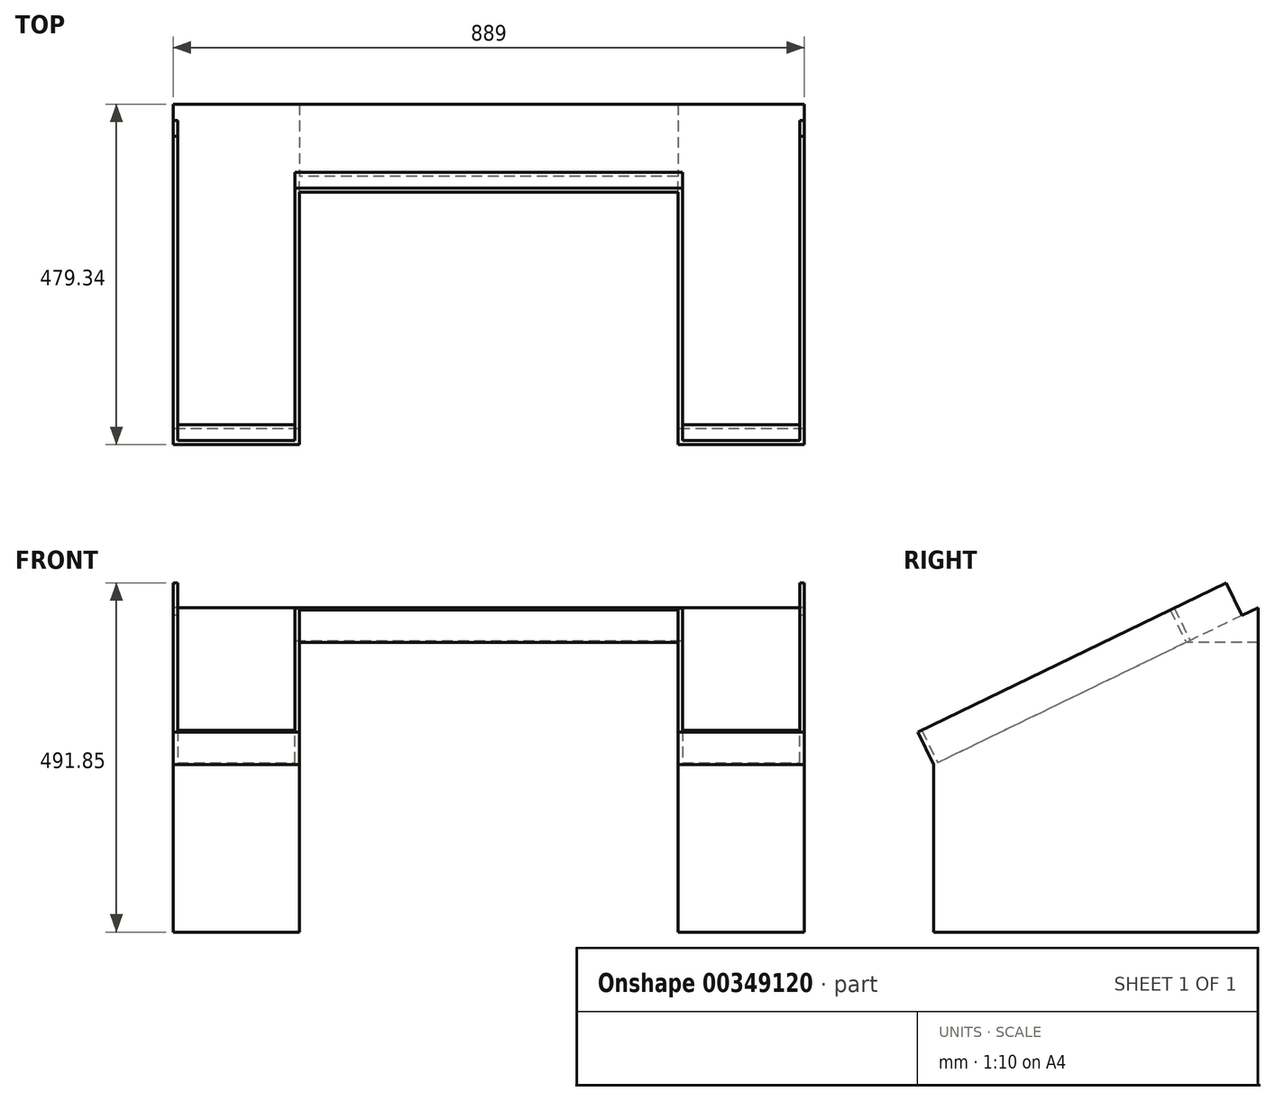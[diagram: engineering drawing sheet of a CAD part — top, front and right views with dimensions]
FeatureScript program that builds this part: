
annotation { "Feature Type Name" : "Feature", "Feature Type Description" : "" }
export const myFeature = defineFeature(function(context is Context, id is Id, definition is map)
    precondition{}
    {
        {
            var Q0;
            Q0=qCreatedBy(makeId("Right.planeOp"),FACE);
            var sketch = newSketch(context, id + "F0", { "sketchPlane" : qUnion([Q0])});
            skLineSegment(sketch, "E0.right", {"start": v(0, 221.43) * mm, "end": v(0, -235.77) * mm});
            skLineSegment(sketch, "E1", {"start": v(0, 221.43) * mm, "end": v(-457.2, 0) * mm});
            skLineSegment(sketch, "E2.right", {"start": v(-457.2, 43.63) * mm, "end": v(-457.2, -235.77) * mm});
            skLineSegment(sketch, "E3", {"start": v(0, -235.77) * mm, "end": v(-457.2, -235.77) * mm});
            skSolve(sketch);
        }
        {
            var Q0;
            Q0 = qSketchRegion(id + "F0", true);
            extrude(context, id + "F1", {"entities" : qUnion([Q0]), "depth" : 889 * mm});
        }
        {
            var Q0;
            Q0=makeQuery(id+"F1.opExtrude","SWEPT_FACE",FACE,{"disambiguationData":[OSD([sQuery(id+"F0.wireOp",EDGE,"E2.right")])]});
            var sketch = newSketch(context, id + "F2", { "sketchPlane" : qUnion([Q0])});
            skLineSegment(sketch, "E4.bottom", {"start": v(177.8, -235.77) * mm, "end": v(711.2, -235.77) * mm});
            skLineSegment(sketch, "E4.top", {"start": v(177.8, 224.7) * mm, "end": v(711.2, 224.7) * mm});
            skLineSegment(sketch, "E4.left", {"start": v(177.8, -235.77) * mm, "end": v(177.8, 224.7) * mm});
            skLineSegment(sketch, "E4.right", {"start": v(711.2, -235.77) * mm, "end": v(711.2, 224.7) * mm});
            skSolve(sketch);
        }
        {
            var Q0;
            {var subQ0=sQuery(id+"F2.wireOp",EDGE,"E4.bottom");Q0=makeQuery(id+"F2.imprint","IMPRINT",FACE,{"disambiguationData":[TD([[makeQuery(id+"F2.imprint","IMPRINT",EDGE,{"derivedFrom":subQ0}),-1.0]])]});}
            var Q1;
            {var subQ0=sQuery(id+"F2.wireOp",EDGE,"E4.top");Q1=makeQuery(id+"F2.imprint","IMPRINT",FACE,{"disambiguationData":[TD([[makeQuery(id+"F2.imprint","IMPRINT",EDGE,{"derivedFrom":subQ0}),-1.0]])]});}
            extrude(context, id + "F3", {"entities" : qUnion([Q0, Q1]), "operationType" : NewBodyOperationType.REMOVE, "oppositeDirection" : true, "depth" : 355.6 * mm});
        }
        {
            var Q0;
            Q0=makeQuery(id+"F1.opExtrude","SWEPT_FACE",FACE,{"disambiguationData":[OSD([sQuery(id+"F0.wireOp",EDGE,"E1")])]});
            var sketch = newSketch(context, id + "F4", { "sketchPlane" : qUnion([Q0])});
            skLineSegment(sketch, "E5", {"start": v(0, 96.52) * mm, "end": v(889, 96.52) * mm});
            skLineSegment(sketch, "E6", {"start": v(889, 96.52) * mm, "end": v(889, -411.48) * mm});
            skLineSegment(sketch, "E7", {"start": v(889, -411.48) * mm, "end": v(711.2, -411.48) * mm});
            skLineSegment(sketch, "E8", {"start": v(711.2, -411.48) * mm, "end": v(711.2, -16.37) * mm});
            skLineSegment(sketch, "E9", {"start": v(711.2, -16.37) * mm, "end": v(177.8, -16.37) * mm});
            skLineSegment(sketch, "E10", {"start": v(177.8, -16.37) * mm, "end": v(177.8, -411.48) * mm});
            skLineSegment(sketch, "E11", {"start": v(177.8, -411.48) * mm, "end": v(0, -411.48) * mm});
            skLineSegment(sketch, "E12", {"start": v(0, -411.48) * mm, "end": v(0, 96.52) * mm});
            skLineSegment(sketch, "E13", {"start": v(6.35, 90.17) * mm, "end": v(6.35, -405.13) * mm});
            skLineSegment(sketch, "E14", {"start": v(6.35, -405.13) * mm, "end": v(171.45, -405.13) * mm});
            skLineSegment(sketch, "E15", {"start": v(171.45, -405.13) * mm, "end": v(171.45, -10.02) * mm});
            skLineSegment(sketch, "E16", {"start": v(171.45, -10.02) * mm, "end": v(717.55, -10.02) * mm});
            skLineSegment(sketch, "E17", {"start": v(717.55, -10.02) * mm, "end": v(717.55, -405.13) * mm});
            skLineSegment(sketch, "E18", {"start": v(717.55, -405.13) * mm, "end": v(882.65, -405.13) * mm});
            skLineSegment(sketch, "E19", {"start": v(882.65, -405.13) * mm, "end": v(882.65, 90.17) * mm});
            skLineSegment(sketch, "E20", {"start": v(882.65, 90.17) * mm, "end": v(6.35, 90.17) * mm});
            skSolve(sketch);
        }
        {
            var Q0;
            Q0 = qSketchRegion(id + "F4", true);
            extrude(context, id + "F5", {"entities" : qUnion([Q0]), "operationType" : NewBodyOperationType.ADD, "depth" : 50.8 * mm});
        }
        {
            var Q0;
            Q0=makeQuery(id+"F5.opExtrude","SWEPT_FACE",FACE,{"disambiguationData":[OSD([sQuery(id+"F4.wireOp",EDGE,"E5")])]});
            extrude(context, id + "F6", {"entities" : qUnion([Q0]), "operationType" : NewBodyOperationType.REMOVE, "oppositeDirection" : true, "depth" : 25.4 * mm});
        }
        {
            var Q0;
            Q0=makeQuery(id+"F3.boolean.opBoolean","COPY",FACE,{"derivedFrom":makeQuery(id+"F3.opExtrude","CAP_FACE",FACE,{"disambiguationData":[OSD([sQuery(id+"F2.wireOp",EDGE,"E4.bottom"),sQuery(id+"F2.wireOp",EDGE,"E4.top"),sQuery(id+"F2.wireOp",EDGE,"E4.left"),sQuery(id+"F2.wireOp",EDGE,"E4.right")])],"isStart":false})});
            extrude(context, id + "F7", {"entities" : qUnion([Q0]), "operationType" : NewBodyOperationType.REMOVE, "endBound" : BoundingType.THROUGH_ALL, "oppositeDirection" : true, "depth" : 25.4 * mm});
        }
    });
